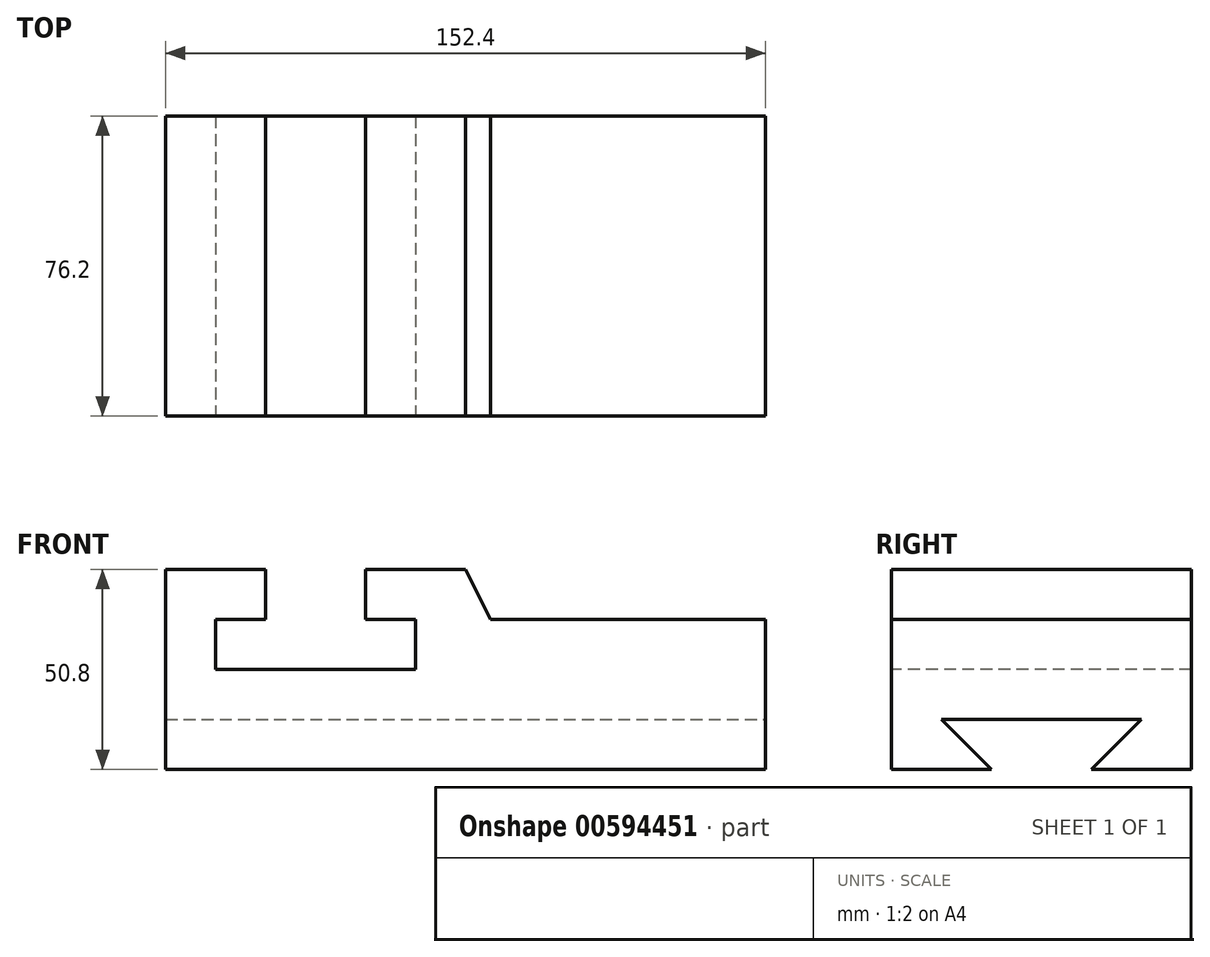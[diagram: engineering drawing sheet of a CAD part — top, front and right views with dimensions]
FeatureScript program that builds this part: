
annotation { "Feature Type Name" : "Feature", "Feature Type Description" : "" }
export const myFeature = defineFeature(function(context is Context, id is Id, definition is map)
    precondition{}
    {
        {
            var Q0;
            Q0=qCreatedBy(makeId("Front.planeOp"),FACE);
            var sketch = newSketch(context, id + "F0", { "sketchPlane" : qUnion([Q0])});
            skLineSegment(sketch, "E0.bottom", {"start": v(0, 0) * mm, "end": v(152.4, 0) * mm});
            skLineSegment(sketch, "E0.top", {"start": v(0, 50.8) * mm, "end": v(152.4, 50.8) * mm});
            skLineSegment(sketch, "E0.left", {"start": v(0, 0) * mm, "end": v(0, 50.8) * mm});
            skLineSegment(sketch, "E0.right", {"start": v(152.4, 0) * mm, "end": v(152.4, 50.8) * mm});
            skSolve(sketch);
        }
        {
            var Q0;
            Q0=makeQuery(id+"F0.imprint","IMPRINT",FACE,{"disambiguationData":[TD([[makeQuery(id+"F0.imprint","IMPRINT",EDGE,{"derivedFrom":sQuery(id+"F0.wireOp",EDGE,"E0.bottom")}),1.0]])]});
            extrude(context, id + "F1", {"entities" : qUnion([Q0]), "oppositeDirection" : true, "depth" : 76.2 * mm, "offsetDistance" : 25.4 * mm});
        }
        {
            var Q0;
            Q0=makeQuery(id+"F1.opExtrude","CAP_FACE",FACE,{"disambiguationData":[OSD([sQuery(id+"F0.wireOp",EDGE,"E0.bottom"),sQuery(id+"F0.wireOp",EDGE,"E0.top"),sQuery(id+"F0.wireOp",EDGE,"E0.left"),sQuery(id+"F0.wireOp",EDGE,"E0.right")])],"isStart":true});
            var sketch = newSketch(context, id + "F2", { "sketchPlane" : qUnion([Q0])});
            skLineSegment(sketch, "E1", {"start": v(25.4, 50.8) * mm, "end": v(25.4, 38.1) * mm});
            skLineSegment(sketch, "E2", {"start": v(25.4, 38.1) * mm, "end": v(12.7, 38.1) * mm});
            skLineSegment(sketch, "E3", {"start": v(12.7, 38.1) * mm, "end": v(12.7, 25.4) * mm});
            skLineSegment(sketch, "E4", {"start": v(12.7, 25.4) * mm, "end": v(63.5, 25.4) * mm});
            skLineSegment(sketch, "E5", {"start": v(63.5, 25.4) * mm, "end": v(63.5, 38.1) * mm});
            skLineSegment(sketch, "E6", {"start": v(63.5, 38.1) * mm, "end": v(50.8, 38.1) * mm});
            skLineSegment(sketch, "E7", {"start": v(50.8, 38.1) * mm, "end": v(50.8, 50.8) * mm});
            skLineSegment(sketch, "E8", {"start": v(50.8, 50.8) * mm, "end": v(25.4, 50.8) * mm});
            skLineSegment(sketch, "E9", {"start": v(82.55, 38.1) * mm, "end": v(76.2, 50.8) * mm});
            skLineSegment(sketch, "E10", {"start": v(82.55, 38.1) * mm, "end": v(152.4, 38.1) * mm});
            skLineSegment(sketch, "E11", {"start": v(152.4, 38.1) * mm, "end": v(152.4, 50.8) * mm});
            skLineSegment(sketch, "E12", {"start": v(152.4, 50.8) * mm, "end": v(76.2, 50.8) * mm});
            skSolve(sketch);
        }
        {
            var Q0;
            Q0=makeQuery(id+"F2.imprint","IMPRINT",FACE,{"disambiguationData":[TD([[makeQuery(id+"F2.imprint","IMPRINT",EDGE,{"derivedFrom":sQuery(id+"F2.wireOp",EDGE,"E1")}),1.0]])]});
            var Q1;
            Q1=makeQuery(id+"F2.imprint","IMPRINT",FACE,{"disambiguationData":[TD([[makeQuery(id+"F2.imprint","IMPRINT",EDGE,{"derivedFrom":sQuery(id+"F2.wireOp",EDGE,"E9")}),-1.0]])]});
            extrude(context, id + "F3", {"entities" : qUnion([Q0, Q1]), "operationType" : NewBodyOperationType.REMOVE, "oppositeDirection" : true, "depth" : 76.2 * mm, "offsetDistance" : 25.4 * mm});
        }
        {
            var Q0;
            Q0=makeQuery(id+"F1.opExtrude","SWEPT_FACE",FACE,{"disambiguationData":[OSD([sQuery(id+"F0.wireOp",EDGE,"E0.right")])]});
            var sketch = newSketch(context, id + "F4", { "sketchPlane" : qUnion([Q0])});
            skPoint(sketch, "E13", {"position": v(25.4, 0) * mm});
            skPoint(sketch, "E14", {"position": v(50.8, 0) * mm});
            skPoint(sketch, "E15", {"position": v(12.7, 12.7) * mm});
            skPoint(sketch, "E16", {"position": v(63.5, 12.7) * mm});
            skLineSegment(sketch, "E17", {"start": v(25.4, 0) * mm, "end": v(12.7, 12.7) * mm});
            skLineSegment(sketch, "E18", {"start": v(12.7, 12.7) * mm, "end": v(63.5, 12.7) * mm});
            skLineSegment(sketch, "E19", {"start": v(63.5, 12.7) * mm, "end": v(50.8, 0) * mm});
            skLineSegment(sketch, "E20", {"start": v(50.8, 0) * mm, "end": v(25.4, 0) * mm});
            skSolve(sketch);
        }
        {
            var Q0;
            Q0=makeQuery(id+"F4.imprint","IMPRINT",FACE,{"disambiguationData":[TD([[makeQuery(id+"F4.imprint","IMPRINT",EDGE,{"derivedFrom":sQuery(id+"F4.wireOp",EDGE,"E17")}),-1.0]])]});
            extrude(context, id + "F5", {"entities" : qUnion([Q0]), "operationType" : NewBodyOperationType.REMOVE, "oppositeDirection" : true, "depth" : 152.4 * mm, "offsetDistance" : 25.4 * mm});
        }
    });
